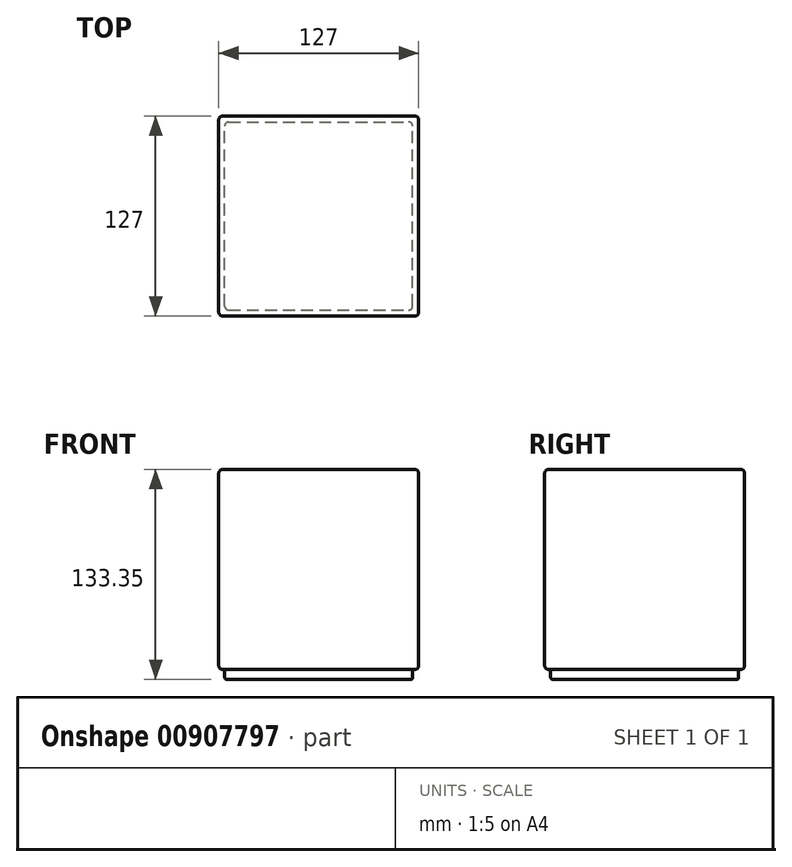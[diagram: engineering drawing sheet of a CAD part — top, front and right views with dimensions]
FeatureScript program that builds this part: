
annotation { "Feature Type Name" : "Feature", "Feature Type Description" : "" }
export const myFeature = defineFeature(function(context is Context, id is Id, definition is map)
    precondition{}
    {
        {
            var Q0;
            Q0=qCreatedBy(makeId("Top.planeOp"),FACE);
            var sketch = newSketch(context, id + "F0", { "sketchPlane" : qUnion([Q0])});
            skLineSegment(sketch, "E0.bottom", {"start": v(63.5, 63.5) * mm, "end": v(-63.5, 63.5) * mm});
            skLineSegment(sketch, "E0.top", {"start": v(63.5, -63.5) * mm, "end": v(-63.5, -63.5) * mm});
            skLineSegment(sketch, "E0.left", {"start": v(63.5, 63.5) * mm, "end": v(63.5, -63.5) * mm});
            skLineSegment(sketch, "E0.right", {"start": v(-63.5, 63.5) * mm, "end": v(-63.5, -63.5) * mm});
            skPoint(sketch, "E0.middle", {"position": v(0, 0) * mm});
            skSolve(sketch);
        }
        {
            var Q0;
            Q0 = qSketchRegion(id + "F0", true);
            extrude(context, id + "F1", {"entities" : qUnion([Q0]), "depth" : 127 * mm, "offsetDistance" : 25.4 * mm});
        }
        {
            var Q0;
            Q0=makeQuery(id+"F1.opExtrude","CAP_FACE",FACE,{"disambiguationData":[OSD([sQuery(id+"F0.wireOp",EDGE,"E0.bottom"),sQuery(id+"F0.wireOp",EDGE,"E0.top"),sQuery(id+"F0.wireOp",EDGE,"E0.left"),sQuery(id+"F0.wireOp",EDGE,"E0.right")])],"isStart":true});
            var sketch = newSketch(context, id + "F2", { "sketchPlane" : qUnion([Q0])});
            skLineSegment(sketch, "E1.bottom", {"start": v(-59.69, 59.69) * mm, "end": v(59.7, 59.69) * mm});
            skLineSegment(sketch, "E1.top", {"start": v(-59.7, -59.69) * mm, "end": v(59.7, -59.69) * mm});
            skLineSegment(sketch, "E1.left", {"start": v(-59.69, 59.69) * mm, "end": v(-59.69, -59.69) * mm});
            skLineSegment(sketch, "E1.right", {"start": v(59.7, 59.69) * mm, "end": v(59.7, -59.69) * mm});
            skPoint(sketch, "E1.middle", {"position": v(0, 0) * mm});
            skSolve(sketch);
        }
        {
            var Q0;
            Q0 = qSketchRegion(id + "F2", true);
            extrude(context, id + "F3", {"entities" : qUnion([Q0]), "operationType" : NewBodyOperationType.ADD, "depth" : 6.35 * mm, "offsetDistance" : 25.4 * mm});
        }
        {
            var Q0;
            Q0=makeQuery(id+"F1.opExtrude","SWEPT_FACE",FACE,{"disambiguationData":[OSD([sQuery(id+"F0.wireOp",EDGE,"E0.bottom")])]});
            var Q1;
            Q1=makeQuery(id+"F1.opExtrude","SWEPT_FACE",FACE,{"disambiguationData":[OSD([sQuery(id+"F0.wireOp",EDGE,"E0.right")])]});
            var Q2;
            Q2=makeQuery(id+"F1.opExtrude","SWEPT_FACE",FACE,{"disambiguationData":[OSD([sQuery(id+"F0.wireOp",EDGE,"E0.top")])]});
            var Q3;
            Q3=makeQuery(id+"F1.opExtrude","SWEPT_FACE",FACE,{"disambiguationData":[OSD([sQuery(id+"F0.wireOp",EDGE,"E0.left")])]});
            fillet(context, id + "F4", {"entities" : qUnion([Q0, Q1, Q2, Q3]), "radius" : 2.54 * mm, "tangentPropagation" : true, "allowEdgeOverflow" : false});
        }
        {
            var Q0;
            Q0=makeQuery(id+"F3.opExtrude","SWEPT_EDGE",EDGE,{"disambiguationData":[OSD([sQuery(id+"F2.wireOp",EDGE,"E1.bottom"),sQuery(id+"F2.wireOp",EDGE,"E1.right")])]});
            var Q1;
            Q1=makeQuery(id+"F3.opExtrude","SWEPT_EDGE",EDGE,{"disambiguationData":[OSD([sQuery(id+"F2.wireOp",EDGE,"E1.bottom"),sQuery(id+"F2.wireOp",EDGE,"E1.left")])]});
            var Q2;
            Q2=makeQuery(id+"F3.opExtrude","SWEPT_EDGE",EDGE,{"disambiguationData":[OSD([sQuery(id+"F2.wireOp",EDGE,"E1.top"),sQuery(id+"F2.wireOp",EDGE,"E1.right")])]});
            var Q3;
            Q3=makeQuery(id+"F3.opExtrude","SWEPT_EDGE",EDGE,{"disambiguationData":[OSD([sQuery(id+"F2.wireOp",EDGE,"E1.top"),sQuery(id+"F2.wireOp",EDGE,"E1.left")])]});
            fillet(context, id + "F5", {"entities" : qUnion([Q0, Q1, Q2, Q3]), "radius" : 2.54 * mm, "tangentPropagation" : true, "allowEdgeOverflow" : false});
        }
        {
            var Q0;
            Q0=makeQuery(id+"F3.opExtrude","CAP_FACE",FACE,{"disambiguationData":[OSD([sQuery(id+"F2.wireOp",EDGE,"E1.bottom"),sQuery(id+"F2.wireOp",EDGE,"E1.top"),sQuery(id+"F2.wireOp",EDGE,"E1.left"),sQuery(id+"F2.wireOp",EDGE,"E1.right")])],"isStart":false});
            fillet(context, id + "F6", {"entities" : qUnion([Q0]), "radius" : 1.27 * mm, "tangentPropagation" : true, "allowEdgeOverflow" : false});
        }
    });
